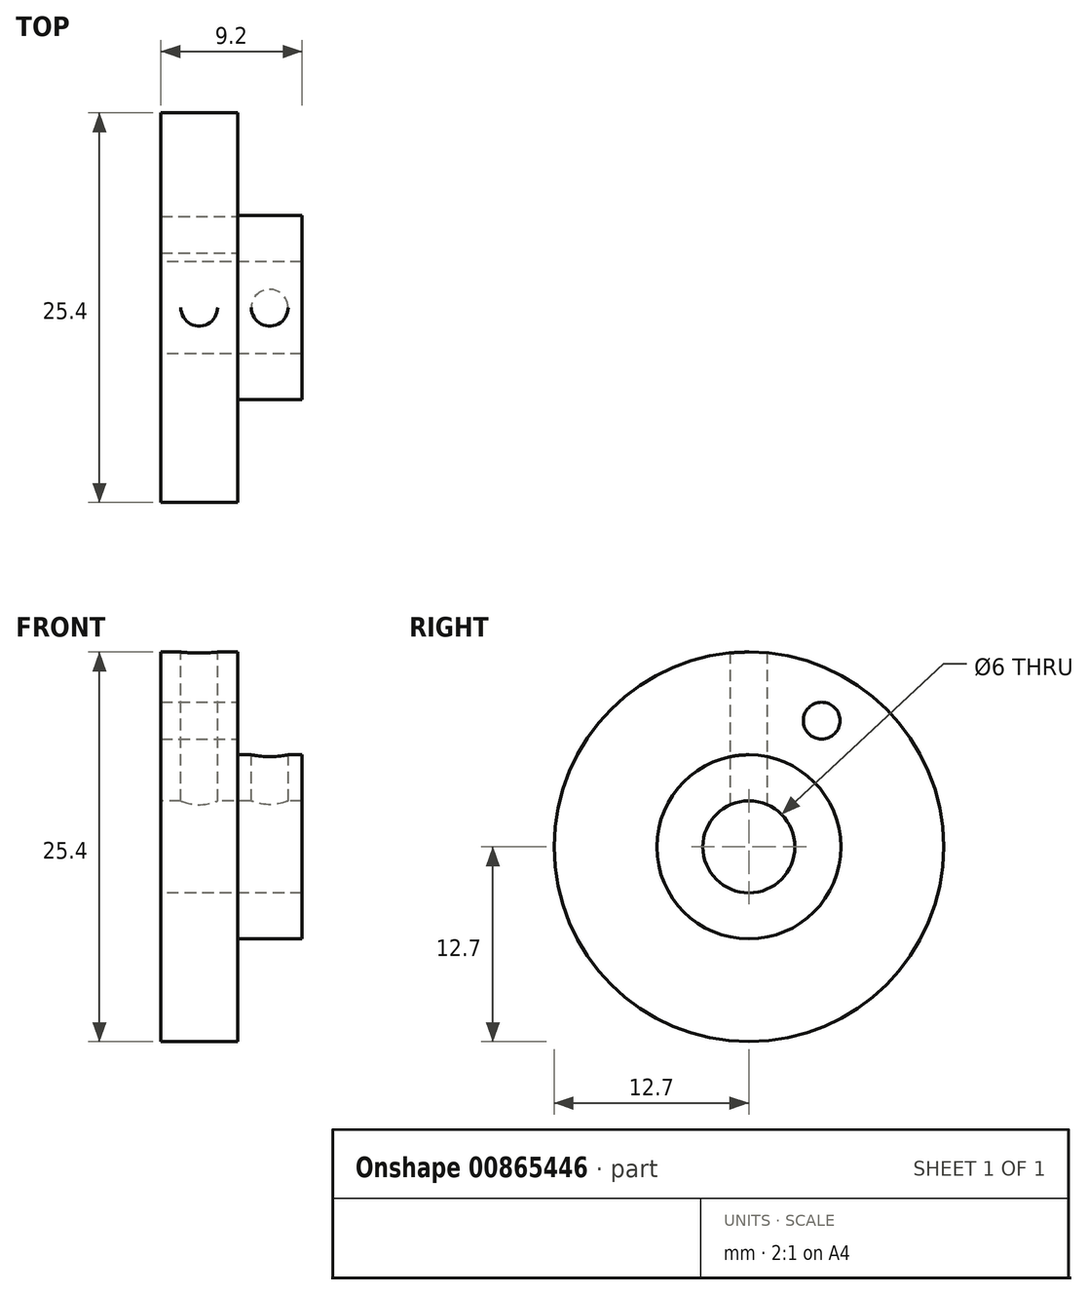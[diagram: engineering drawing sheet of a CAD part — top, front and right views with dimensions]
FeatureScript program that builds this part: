
annotation { "Feature Type Name" : "Feature", "Feature Type Description" : "" }
export const myFeature = defineFeature(function(context is Context, id is Id, definition is map)
    precondition{}
    {
        {
            var Q0;
            Q0=qCreatedBy(makeId("Front.planeOp"),FACE);
            var sketch = newSketch(context, id + "F0", { "sketchPlane" : qUnion([Q0])});
            skLineSegment(sketch, "E0", {"start": v(-2.5, 0) * mm, "end": v(6.7, 0) * mm, "construction": true});
            skLineSegment(sketch, "E1", {"start": v(-2.5, 3) * mm, "end": v(-2.5, 12.7) * mm});
            skLineSegment(sketch, "E2", {"start": v(-2.5, 12.7) * mm, "end": v(2.5, 12.7) * mm});
            skLineSegment(sketch, "E3", {"start": v(2.5, 12.7) * mm, "end": v(2.5, 6) * mm});
            skLineSegment(sketch, "E4", {"start": v(2.5, 6) * mm, "end": v(6.7, 6) * mm});
            skLineSegment(sketch, "E5", {"start": v(6.7, 6) * mm, "end": v(6.7, 3) * mm});
            skLineSegment(sketch, "E6", {"start": v(6.7, 3) * mm, "end": v(-2.5, 3) * mm});
            skPoint(sketch, "E7", {"position": v(0, 12.7) * mm});
            skPoint(sketch, "E8", {"position": v(4.6, 6) * mm});
            skSolve(sketch);
        }
        {
            var Q0;
            Q0=qSketchRegion(id+"F0",true);
            var Q1;
            Q1=sQuery(id+"F0.wireOp",EDGE,"E0");
            revolve(context, id + "F1", {"entities" : qUnion([Q0]), "axis" : qUnion([Q1]), "revolveType" : RevolveType.FULL});
        }
        {
            var Q0;
            Q0=makeQuery(id+"F1.opRevolve","SWEPT_FACE",FACE,{"disambiguationData":[OSD([sQuery(id+"F0.wireOp",EDGE,"E3")])]});
            var sketch = newSketch(context, id + "F2", { "sketchPlane" : qUnion([Q0])});
            skLineSegment(sketch, "E9", {"start": v(0, 0) * mm, "end": v(4.75, 8.23) * mm, "construction": true});
            skSolve(sketch);
        }
        {
            var Q0;
            Q0=sQuery(id+"F2.wireOp",VERTEX,"E9.end");
            var Q1;
            Q1=makeQuery(id+"F1.opRevolve","SWEPT_BODY",BODY,{"disambiguationData":[OSD([sQuery(id+"F0.wireOp",EDGE,"E1"),sQuery(id+"F0.wireOp",EDGE,"E2"),sQuery(id+"F0.wireOp",EDGE,"E3"),sQuery(id+"F0.wireOp",EDGE,"E4"),sQuery(id+"F0.wireOp",EDGE,"E5"),sQuery(id+"F0.wireOp",EDGE,"E6")])]});
            hole(context, id + "F3", {"style" : HoleStyle.SIMPLE, "endStyle" : HoleEndStyle.THROUGH, "standardTappedOrClearance" : lookupTablePath({ "standard" : "ISO", "engagement" : "75%", "pitch" : "0.6 mm", "size" : "M3", "type" : "Tapped" }), "standardBlindInLast" : lookupTablePath({ "standard" : "ISO", "engagement" : "75%", "pitch" : "0.6 mm", "size" : "M3", "type" : "Tapped" }), "holeDiameter" : 2.4 * mm, "showTappedDepth" : true, "tappedDepth" : 12 * mm, "tapClearance" : 3, "locations" : qUnion([Q0]), "scope" : qUnion([Q1])});
        }
        {
            var Q0;
            Q0=qCreatedBy(makeId("Top.planeOp"),FACE);
            var Q1;
            Q1=sQuery(id+"F0.wireOp",VERTEX,"E7");
            cPlane(context, id + "F4", {"entities" : qUnion([Q0, Q1]), "cplaneType" : CPlaneType.PLANE_POINT, "offset" : 25 * mm, "width" : 150 * mm, "height" : 150 * mm});
        }
        {
            var Q0;
            Q0=qCreatedBy(id+"F4.planeOp",FACE);
            var sketch = newSketch(context, id + "F5", { "sketchPlane" : qUnion([Q0])});
            skPoint(sketch, "E10", {"position": v(0, 0) * mm});
            skSolve(sketch);
        }
        {
            var Q0;
            Q0=sQuery(id+"F5.wireOp",VERTEX,"E10");
            var Q1;
            Q1=makeQuery(id+"F1.opRevolve","SWEPT_BODY",BODY,{"disambiguationData":[OSD([sQuery(id+"F0.wireOp",EDGE,"E1"),sQuery(id+"F0.wireOp",EDGE,"E2"),sQuery(id+"F0.wireOp",EDGE,"E3"),sQuery(id+"F0.wireOp",EDGE,"E4"),sQuery(id+"F0.wireOp",EDGE,"E5"),sQuery(id+"F0.wireOp",EDGE,"E6")])]});
            hole(context, id + "F6", {"style" : HoleStyle.SIMPLE, "endStyle" : HoleEndStyle.BLIND, "standardTappedOrClearance" : lookupTablePath({ "standard" : "ISO", "engagement" : "75%", "pitch" : "0.6 mm", "size" : "M3", "type" : "Tapped" }), "standardBlindInLast" : lookupTablePath({ "standard" : "ISO", "engagement" : "75%", "pitch" : "0.6 mm", "size" : "M3", "type" : "Tapped" }), "holeDiameter" : 2.4 * mm, "showTappedDepth" : true, "holeDepth" : 25.4 / 2 * mm, "tappedDepth" : 10.9 * mm, "tapClearance" : 3, "locations" : qUnion([Q0]), "scope" : qUnion([Q1])});
        }
        {
            var Q0;
            Q0=qCreatedBy(makeId("Top.planeOp"),FACE);
            var Q1;
            Q1=sQuery(id+"F0.wireOp",VERTEX,"E8");
            cPlane(context, id + "F7", {"entities" : qUnion([Q0, Q1]), "cplaneType" : CPlaneType.PLANE_POINT, "offset" : 25 * mm, "width" : 150 * mm, "height" : 150 * mm});
        }
        {
            var Q0;
            Q0=qCreatedBy(id+"F7.planeOp",FACE);
            var sketch = newSketch(context, id + "F8", { "sketchPlane" : qUnion([Q0])});
            skPoint(sketch, "E11", {"position": v(4.6, 0) * mm});
            skSolve(sketch);
        }
        {
            var Q0;
            Q0=sQuery(id+"F8.wireOp",VERTEX,"E11");
            var Q1;
            Q1=makeQuery(id+"F1.opRevolve","SWEPT_BODY",BODY,{"disambiguationData":[OSD([sQuery(id+"F0.wireOp",EDGE,"E1"),sQuery(id+"F0.wireOp",EDGE,"E2"),sQuery(id+"F0.wireOp",EDGE,"E3"),sQuery(id+"F0.wireOp",EDGE,"E4"),sQuery(id+"F0.wireOp",EDGE,"E5"),sQuery(id+"F0.wireOp",EDGE,"E6")])]});
            hole(context, id + "F9", {"style" : HoleStyle.SIMPLE, "endStyle" : HoleEndStyle.BLIND, "standardTappedOrClearance" : lookupTablePath({ "standard" : "ISO", "engagement" : "75%", "pitch" : "0.6 mm", "size" : "M3", "type" : "Tapped" }), "standardBlindInLast" : lookupTablePath({ "standard" : "ISO", "engagement" : "75%", "pitch" : "0.6 mm", "size" : "M3", "type" : "Tapped" }), "holeDiameter" : 2.4 * mm, "showTappedDepth" : true, "holeDepth" : 5 * mm, "tappedDepth" : 3.2 * mm, "tapClearance" : 3, "locations" : qUnion([Q0]), "scope" : qUnion([Q1])});
        }
    });
